# Revit family: FP-Revit20-Washer D
name_source: partatom
category: Specialty Equipment
units: mm (PartAtom-declared; Revit-internal decimal feet)

## family parameters
Always vertical = Yes
Cut with Voids When Loaded = Yes
OmniClass Number = 23.45.70.11.11
OmniClass Title = Residential Laundry Equipment
Part Type = Normal
Room Calculation Point = No
Round Connector Dimension = Use Diameter
Shared = Yes
Work Plane-Based = No

## types (6) — shared parameters
Cavity - Width = 622 mm  [stored 2.04068 ft]
Chassis - Height = 822 mm  [stored 2.69685 ft]
Chassis - Width = 602 mm  [stored 1.97507 ft]
Connector Description - Electrical = 220 – 240 V, 50 Hz, 10 A service
Connector Description - Sanitary = Drain to Standpipe, Max 1000mm high, Min 600mm high
Connector Description - Water = Cold + Hot, Max 1 MPa (150psi) Min 50 kPa (7psi), Min 6 Litres/min
Manufacturer = Fisher & Paykel Appliances Ltd
Material - Body = Fisher & Paykel - Grey
Material - Display Panel = Fisher & Paykel - Black
Material - Door Glass = Fisher & Paykel - Glass, Black
Material - Door Trim = Fisher & Paykel - Steel, Chrome Plated
Product - Width = 595 mm  [stored 1.9521 ft]
Style - Control Panel = Control Panel WH DH : D
Visibility - Clearance Required = Yes
zero-valued in all types: Default Elevation

## per-type parameters (varying)
| type | Cavity - Depth | Chassis - Depth | Description | Material - Buttons and Dials | Material - Control Panel | Material - Front | Product - Depth |
| WH1260DG5 | 668 mm  [stored 2.1916 ft] | 583 mm | 12kg Series 7 Contemporary Front Loader Washer, Graphite | Fisher & Paykel - Stainless Steel (Dark) | Fisher & Paykel - Glass, Graphite | Fisher & Paykel - Graphite | 661 mm  [stored 2.16864 ft] |
| WH1260D5 | 668 mm  [stored 2.1916 ft] | 583 mm | 12kg Series 7 Contemporary Front Loader Washer, White | Fisher & Paykel - Stainless Steel | Fisher & Paykel - Glass, Silver | Fisher & Paykel - White | 661 mm  [stored 2.16864 ft] |
| WH1060D5 | 668 mm  [stored 2.1916 ft] | 583 mm | 10kg Series 7 Contemporary Front Loader Washer, White | Fisher & Paykel - Stainless Steel | Fisher & Paykel - Glass, Silver | Fisher & Paykel - White | 661 mm  [stored 2.16864 ft] |
| WH1060DG5 | 668 mm  [stored 2.1916 ft] | 583 mm | 10kg Series 7 Contemporary Front Loader Washer, White | Fisher & Paykel - Stainless Steel (Dark) | Fisher & Paykel - Glass, Graphite | Fisher & Paykel - Graphite | 661 mm  [stored 2.16864 ft] |
| WH9060D5 | 600 mm  [stored 1.9685 ft] | 515 mm  [stored 1.68963 ft] | 9kg Series 7 Contemporary Front Loader Washer, White | Fisher & Paykel - Stainless Steel | Fisher & Paykel - Glass, Silver | Fisher & Paykel - White | 593 mm  [stored 1.94554 ft] |
| WH9060DG5 | 600 mm  [stored 1.9685 ft] | 515 mm  [stored 1.68963 ft] | 9kg Series 7 Contemporary Front Loader Washer, Graphite | Fisher & Paykel - Stainless Steel (Dark) | Fisher & Paykel - Glass, Graphite | Fisher & Paykel - Graphite | 593 mm  [stored 1.94554 ft] |

note: column(s) folded — value = type name in every type: Model

note: [stored X ft] marks values corroborated as IEEE doubles in the binary element streams (Revit-internal decimal feet)

## geometry (parser evidence)
native form markers: Sweep x6
no freeform markers — native parametric forms only
